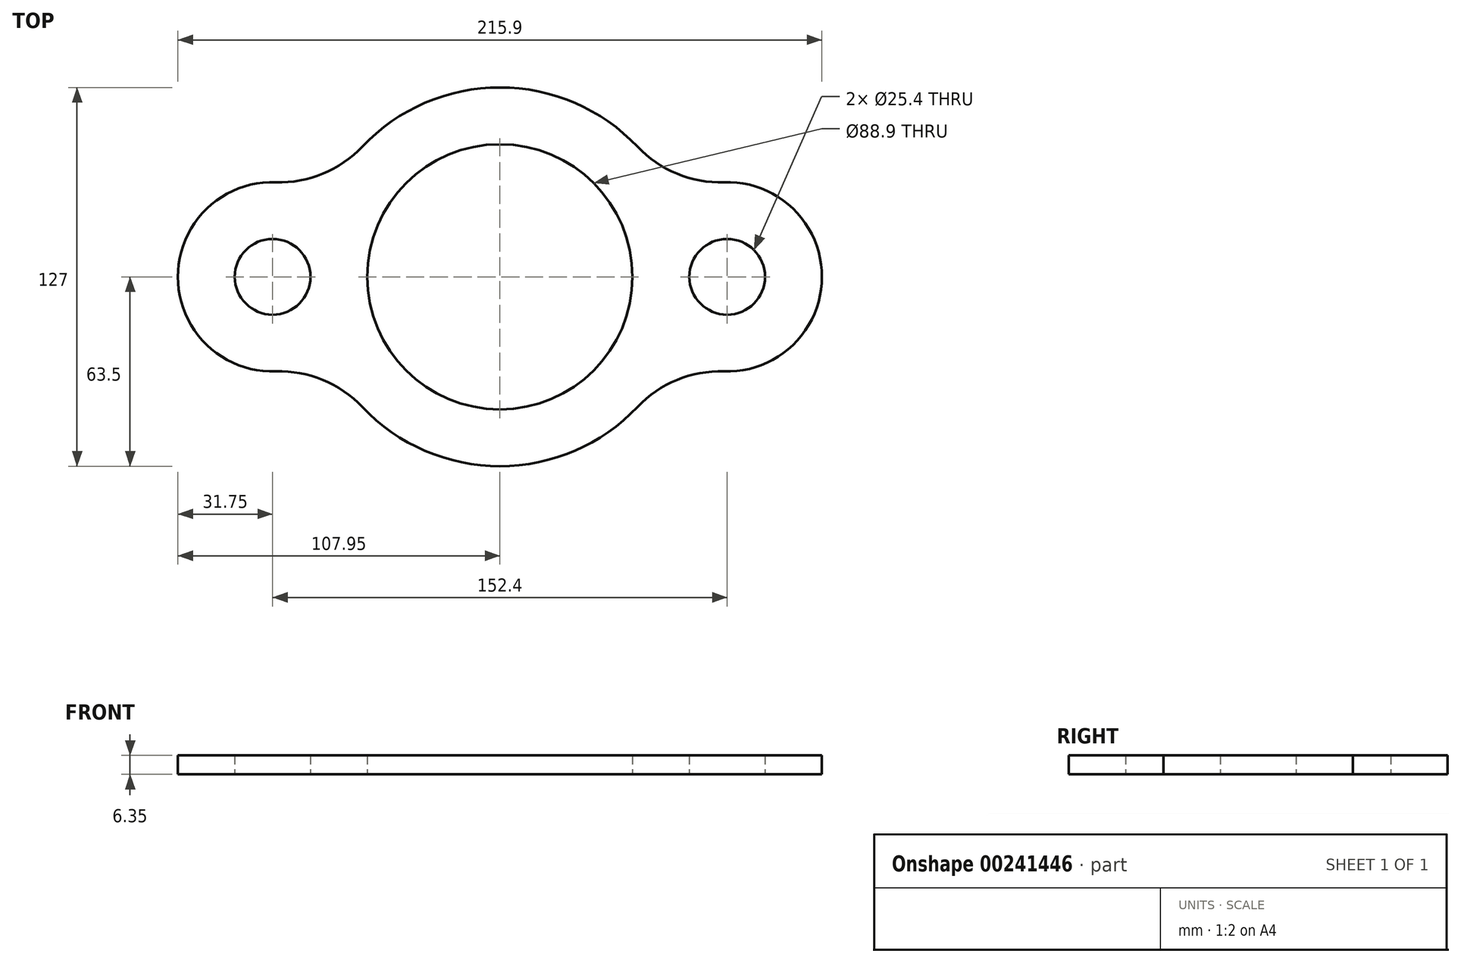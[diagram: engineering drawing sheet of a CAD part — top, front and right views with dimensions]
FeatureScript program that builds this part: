
annotation { "Feature Type Name" : "Feature", "Feature Type Description" : "" }
export const myFeature = defineFeature(function(context is Context, id is Id, definition is map)
    precondition{}
    {
        {
            var Q0;
            Q0=qCreatedBy(makeId("Top.planeOp"),FACE);
            var sketch = newSketch(context, id + "F0", { "sketchPlane" : qUnion([Q0])});
            skCircle(sketch, "E0", {"center": v(0, 0) * mm, "radius": 44.45 * mm});
            skArc(sketch, "E1", {"start": v(46.14, 43.63) * mm, "mid": v(0, 63.5) * mm, "end": v(-46.14, 43.63) * mm});
            skCircle(sketch, "E2", {"center": v(-76.2, 0) * mm, "radius": 12.7 * mm});
            skCircle(sketch, "E3", {"center": v(76.2, 0) * mm, "radius": 12.7 * mm});
            skArc(sketch, "E4", {"start": v(-75.12, 31.73) * mm, "mid": v(-107.95, 0) * mm, "end": v(-75.12, -31.73) * mm});
            skArc(sketch, "E5", {"start": v(75.12, -31.73) * mm, "mid": v(107.95, 0) * mm, "end": v(75.12, 31.73) * mm});
            skArc(sketch, "E6.trimOffspring", {"start": v(-46.14, -43.63) * mm, "mid": v(0, -63.5) * mm, "end": v(46.14, -43.63) * mm});
            skPoint(sketch, "E7.visualSharp", {"position": v(-57.94, 25.98) * mm});
            skArc(sketch, "E7.filletArc", {"start": v(-75.12, 31.73) * mm, "mid": v(-59.35, 34.56) * mm, "end": v(-46.14, 43.63) * mm});
            skPoint(sketch, "E8.visualSharp", {"position": v(-57.94, -25.98) * mm});
            skArc(sketch, "E8.filletArc", {"start": v(-46.14, -43.63) * mm, "mid": v(-59.35, -34.56) * mm, "end": v(-75.12, -31.73) * mm});
            skPoint(sketch, "E9.visualSharp", {"position": v(57.94, -25.98) * mm});
            skArc(sketch, "E9.filletArc", {"start": v(75.12, -31.73) * mm, "mid": v(59.35, -34.56) * mm, "end": v(46.14, -43.63) * mm});
            skPoint(sketch, "E10.visualSharp", {"position": v(57.94, 25.98) * mm});
            skArc(sketch, "E10.filletArc", {"start": v(46.14, 43.63) * mm, "mid": v(59.35, 34.56) * mm, "end": v(75.12, 31.73) * mm});
            skSolve(sketch);
        }
        {
            var Q0;
            Q0 = qSketchRegion(id + "F0", true);
            extrude(context, id + "F1", {"entities" : qUnion([Q0]), "depth" : 6.35 * mm});
        }
    });
